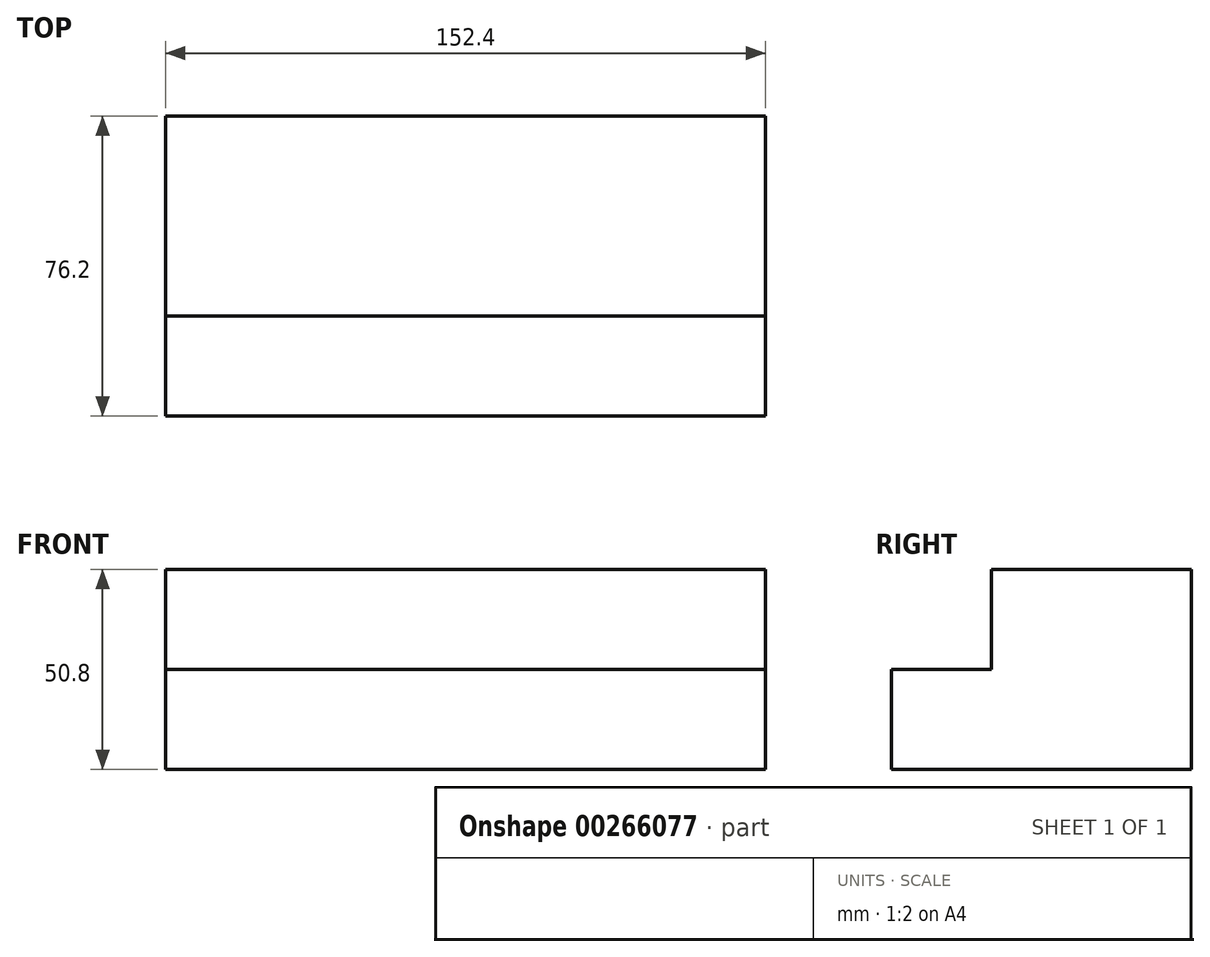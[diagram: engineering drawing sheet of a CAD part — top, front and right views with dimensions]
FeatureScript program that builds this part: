
annotation { "Feature Type Name" : "Feature", "Feature Type Description" : "" }
export const myFeature = defineFeature(function(context is Context, id is Id, definition is map)
    precondition{}
    {
        {
            var Q0;
            Q0=qCreatedBy(makeId("Front.planeOp"),FACE);
            var sketch = newSketch(context, id + "F0", { "sketchPlane" : qUnion([Q0])});
            skLineSegment(sketch, "E0.bottom", {"start": v(-47.71, 14.95) * mm, "end": v(104.69, 14.95) * mm});
            skLineSegment(sketch, "E0.top", {"start": v(-47.71, 65.75) * mm, "end": v(104.69, 65.75) * mm});
            skLineSegment(sketch, "E0.left", {"start": v(-47.71, 14.95) * mm, "end": v(-47.71, 65.75) * mm});
            skLineSegment(sketch, "E0.right", {"start": v(104.69, 14.95) * mm, "end": v(104.69, 65.75) * mm});
            skSolve(sketch);
        }
        {
            var Q0;
            Q0 = qSketchRegion(id + "F0", true);
            extrude(context, id + "F1", {"entities" : qUnion([Q0]), "depth" : 76.2 * mm});
        }
        {
            var Q0;
            Q0=makeQuery(id+"F1.opExtrude","SWEPT_FACE",FACE,{"disambiguationData":[OSD([sQuery(id+"F0.wireOp",EDGE,"E0.right")])]});
            var sketch = newSketch(context, id + "F2", { "sketchPlane" : qUnion([Q0])});
            skLineSegment(sketch, "E1.bottom", {"start": v(-76.2, 65.75) * mm, "end": v(-50.8, 65.75) * mm});
            skLineSegment(sketch, "E1.top", {"start": v(-76.2, 40.35) * mm, "end": v(-50.8, 40.35) * mm});
            skLineSegment(sketch, "E1.left", {"start": v(-76.2, 65.75) * mm, "end": v(-76.2, 40.35) * mm});
            skLineSegment(sketch, "E1.right", {"start": v(-50.8, 65.75) * mm, "end": v(-50.8, 40.35) * mm});
            skSolve(sketch);
        }
        {
            var Q0;
            Q0=makeQuery(id+"F2.imprint","IMPRINT",FACE,{"disambiguationData":[TD([[makeQuery(id+"F2.imprint","IMPRINT",EDGE,{"derivedFrom":sQuery(id+"F2.wireOp",EDGE,"E1.bottom")}),-1.0]])]});
            extrude(context, id + "F3", {"entities" : qUnion([Q0]), "operationType" : NewBodyOperationType.REMOVE, "endBound" : BoundingType.UP_TO_NEXT, "oppositeDirection" : true, "depth" : 25.4 * mm});
        }
    });
